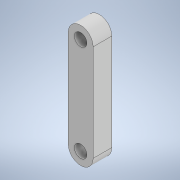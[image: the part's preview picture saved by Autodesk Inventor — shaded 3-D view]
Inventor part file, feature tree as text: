
AUTODESK INVENTOR PART (.ipt)
format: ipt  version: 2021 (Build 250183000, 183)  size: 106,496 bytes
history: native  units: mm
features: extrude x1, sketch x1
ambient origin geometry x8: Origin, YZ Plane, XZ Plane, XY Plane, X Axis, Y Axis, Z Axis, Center Point
bodies: Solid1 (feature_tree)
feature tree (2):
  extrude  "Extrusion1"  Depth=8.0mm
  sketch  "Sketch1"  dims[d0=4.0mm d1=8.0mm d2=4.0mm d3=8.0mm d4=6.0mm d5=0.0mm d6=31.0mm]
